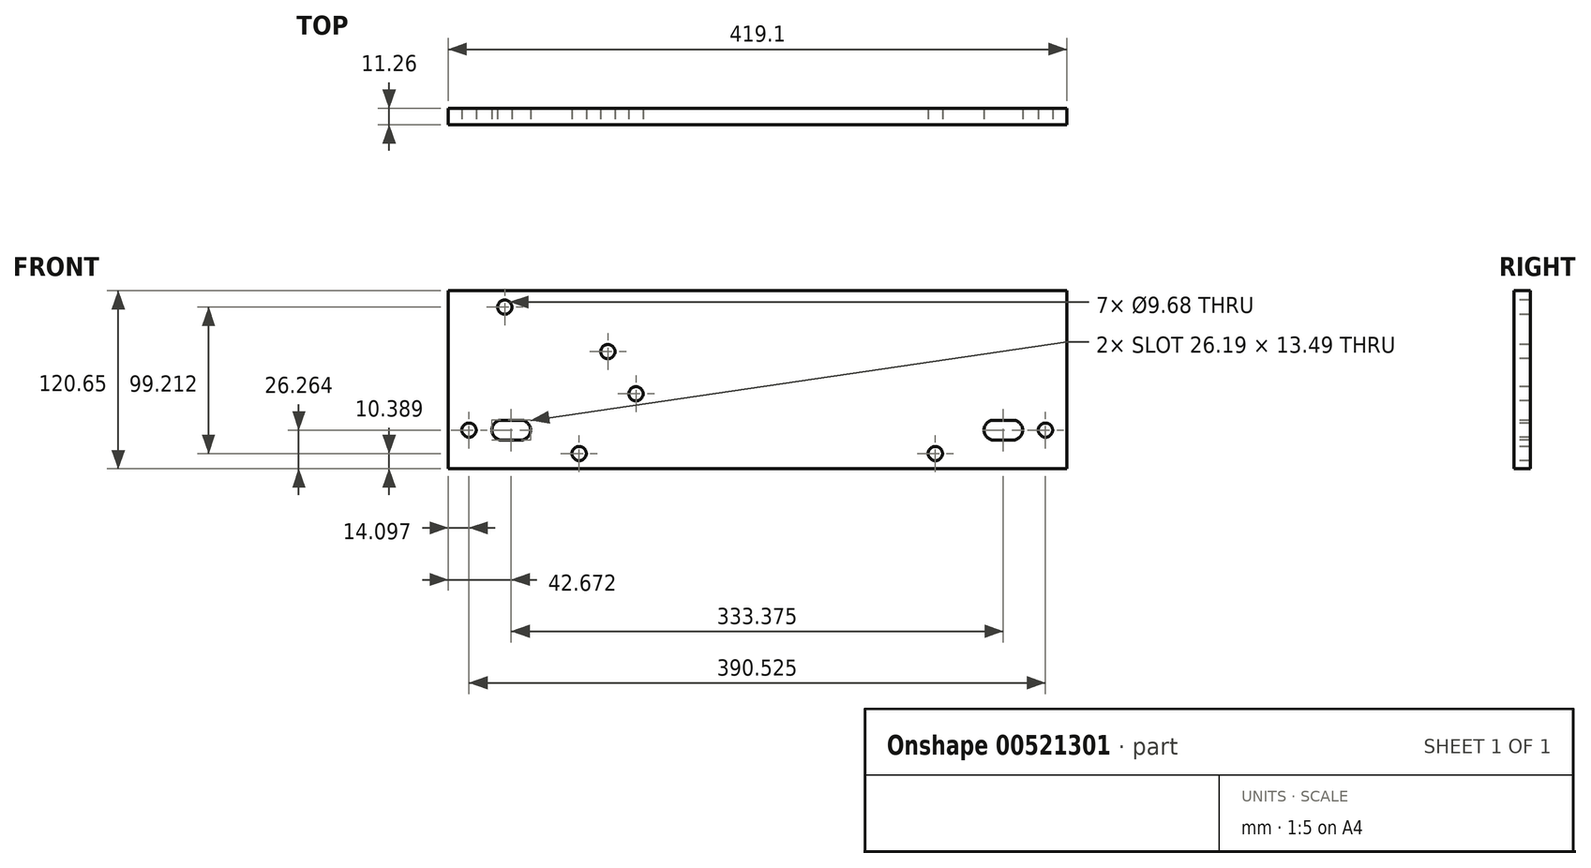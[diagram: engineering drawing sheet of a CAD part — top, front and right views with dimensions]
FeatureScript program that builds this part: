
annotation { "Feature Type Name" : "Feature", "Feature Type Description" : "" }
export const myFeature = defineFeature(function(context is Context, id is Id, definition is map)
    precondition{}
    {
        {
            var Q0;
            Q0=qCreatedBy(makeId("Front.planeOp"),FACE);
            var sketch = newSketch(context, id + "F0", { "sketchPlane" : qUnion([Q0])});
            skLineSegment(sketch, "E0", {"start": v(0, 0) * mm, "end": v(0, 120.65) * mm});
            skLineSegment(sketch, "E1", {"start": v(0, 120.65) * mm, "end": v(419.1, 120.65) * mm});
            skLineSegment(sketch, "E2", {"start": v(0, 0) * mm, "end": v(419.1, 0) * mm});
            skLineSegment(sketch, "E3", {"start": v(419.1, 0) * mm, "end": v(419.1, 120.65) * mm});
            skSolve(sketch);
        }
        {
            var Q0;
            Q0 = qSketchRegion(id + "F0", true);
            extrude(context, id + "F1", {"entities" : qUnion([Q0]), "endBound" : BoundingType.SYMMETRIC, "depth" : 11.25 * mm, "offsetDistance" : 25.4 * mm});
        }
        {
            var Q0;
            Q0=makeQuery(id+"F1.opExtrude","CAP_FACE",FACE,{"disambiguationData":[OSD([sQuery(id+"F0.wireOp",EDGE,"E0"),sQuery(id+"F0.wireOp",EDGE,"E1"),sQuery(id+"F0.wireOp",EDGE,"E2"),sQuery(id+"F0.wireOp",EDGE,"E3")])],"isStart":false});
            var sketch = newSketch(context, id + "F2", { "sketchPlane" : qUnion([Q0])});
            skCircle(sketch, "E4", {"center": v(14.1, 26.26) * mm, "radius": 4.84 * mm});
            skCircle(sketch, "E5", {"center": v(38.3, 109.6) * mm, "radius": 4.84 * mm});
            skCircle(sketch, "E6", {"center": v(108.15, 79.45) * mm, "radius": 4.84 * mm});
            skCircle(sketch, "E7", {"center": v(330, 10.39) * mm, "radius": 4.84 * mm});
            skCircle(sketch, "E8", {"center": v(88.7, 10.39) * mm, "radius": 4.84 * mm});
            skCircle(sketch, "E9", {"center": v(127.2, 50.88) * mm, "radius": 4.84 * mm});
            skCircle(sketch, "E10", {"center": v(404.62, 26.26) * mm, "radius": 4.84 * mm});
            skSolve(sketch);
        }
        {
            var Q0;
            Q0 = qSketchRegion(id + "F2", true);
            extrude(context, id + "F3", {"entities" : qUnion([Q0]), "operationType" : NewBodyOperationType.REMOVE, "endBound" : BoundingType.THROUGH_ALL, "oppositeDirection" : true, "depth" : 25.4 * mm, "offsetDistance" : 25.4 * mm});
        }
        {
            var Q0;
            Q0=makeQuery(id+"F1.opExtrude","CAP_FACE",FACE,{"disambiguationData":[OSD([sQuery(id+"F0.wireOp",EDGE,"E0"),sQuery(id+"F0.wireOp",EDGE,"E1"),sQuery(id+"F0.wireOp",EDGE,"E2"),sQuery(id+"F0.wireOp",EDGE,"E3")])],"isStart":false});
            var sketch = newSketch(context, id + "F4", { "sketchPlane" : qUnion([Q0])});
            skArc(sketch, "E11", {"start": v(36.32, 33) * mm, "mid": v(29.58, 26.26) * mm, "end": v(36.32, 19.52) * mm});
            skLineSegment(sketch, "E12", {"start": v(36.32, 33) * mm, "end": v(49.02, 33) * mm});
            skLineSegment(sketch, "E13", {"start": v(36.32, 19.52) * mm, "end": v(49.02, 19.52) * mm});
            skArc(sketch, "E14.trimOffspring", {"start": v(49.02, 19.52) * mm, "mid": v(55.77, 26.26) * mm, "end": v(49.02, 33) * mm});
            skArc(sketch, "E15", {"start": v(369.7, 33) * mm, "mid": v(362.95, 26.26) * mm, "end": v(369.7, 19.52) * mm});
            skLineSegment(sketch, "E16", {"start": v(369.7, 33) * mm, "end": v(382.4, 33) * mm});
            skLineSegment(sketch, "E17", {"start": v(369.7, 19.52) * mm, "end": v(382.4, 19.52) * mm});
            skArc(sketch, "E18.trimOffspring", {"start": v(382.4, 19.52) * mm, "mid": v(389.14, 26.26) * mm, "end": v(382.4, 33) * mm});
            skSolve(sketch);
        }
        {
            var Q0;
            Q0 = qSketchRegion(id + "F4", true);
            extrude(context, id + "F5", {"entities" : qUnion([Q0]), "operationType" : NewBodyOperationType.REMOVE, "endBound" : BoundingType.THROUGH_ALL, "oppositeDirection" : true, "depth" : 25.4 * mm, "offsetDistance" : 25.4 * mm});
        }
    });
